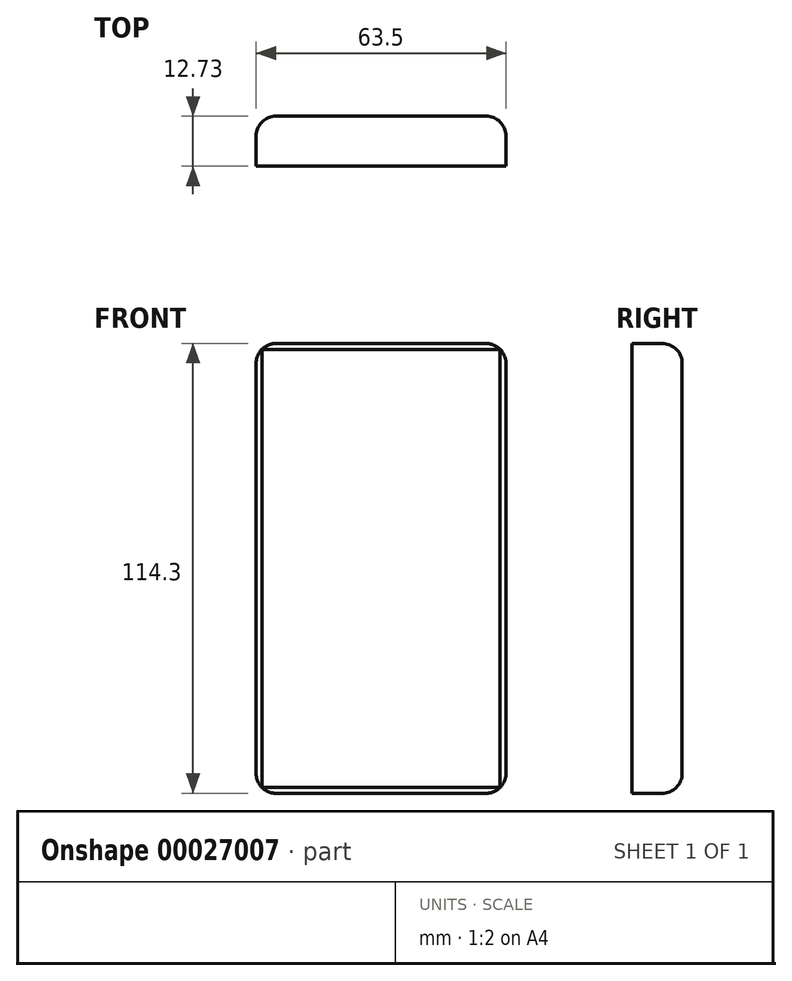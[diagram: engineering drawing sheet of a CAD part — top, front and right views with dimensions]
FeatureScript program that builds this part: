
annotation { "Feature Type Name" : "Feature", "Feature Type Description" : "" }
export const myFeature = defineFeature(function(context is Context, id is Id, definition is map)
    precondition{}
    {
        {
            var Q0;
            Q0=qCreatedBy(makeId("Front.planeOp"),FACE);
            var sketch = newSketch(context, id + "F0", { "sketchPlane" : qUnion([Q0])});
            skLineSegment(sketch, "E0.bottom", {"start": v(-36.96, 45.78) * mm, "end": v(26.54, 45.78) * mm});
            skLineSegment(sketch, "E0.top", {"start": v(-36.96, -68.52) * mm, "end": v(26.54, -68.52) * mm});
            skLineSegment(sketch, "E0.left", {"start": v(-36.96, 45.78) * mm, "end": v(-36.96, -68.52) * mm});
            skLineSegment(sketch, "E0.right", {"start": v(26.54, 45.78) * mm, "end": v(26.54, -68.52) * mm});
            skSolve(sketch);
        }
        {
            var Q0;
            Q0=makeQuery(id+"F0.imprint","IMPRINT",FACE,{"disambiguationData":[TD([[makeQuery(id+"F0.imprint","IMPRINT",EDGE,{"derivedFrom":sQuery(id+"F0.wireOp",EDGE,"E0.bottom")}),-1.0]])]});
            extrude(context, id + "F1", {"entities" : qUnion([Q0]), "depth" : 12.7 * mm});
        }
        {
            var Q0;
            Q0=makeQuery(id+"F1.opExtrude","SWEPT_EDGE",EDGE,{"disambiguationData":[OSD([sQuery(id+"F0.wireOp",EDGE,"E0.bottom"),sQuery(id+"F0.wireOp",EDGE,"E0.right")])]});
            var Q1;
            Q1=makeQuery(id+"F1.opExtrude","SWEPT_EDGE",EDGE,{"disambiguationData":[OSD([sQuery(id+"F0.wireOp",EDGE,"E0.top"),sQuery(id+"F0.wireOp",EDGE,"E0.right")])]});
            var Q2;
            Q2=makeQuery(id+"F1.opExtrude","SWEPT_EDGE",EDGE,{"disambiguationData":[OSD([sQuery(id+"F0.wireOp",EDGE,"E0.top"),sQuery(id+"F0.wireOp",EDGE,"E0.left")])]});
            var Q3;
            Q3=makeQuery(id+"F1.opExtrude","SWEPT_EDGE",EDGE,{"disambiguationData":[OSD([sQuery(id+"F0.wireOp",EDGE,"E0.bottom"),sQuery(id+"F0.wireOp",EDGE,"E0.left")])]});
            fillet(context, id + "F2", {"entities" : qUnion([Q0, Q1, Q2, Q3]), "radius" : 5.08 * mm, "allowEdgeOverflow" : false});
        }
        {
            var Q0;
            Q0=makeQuery(id+"F1.opExtrude","CAP_EDGE",EDGE,{"disambiguationData":[OSD([sQuery(id+"F0.wireOp",EDGE,"E0.right")])],"isStart":true});
            fillet(context, id + "F3", {"entities" : qUnion([Q0]), "radius" : 5.08 * mm, "tangentPropagation" : true, "allowEdgeOverflow" : false});
        }
        {
            var Q0;
            Q0=makeQuery(id+"F1.opExtrude","CAP_FACE",FACE,{"disambiguationData":[OSD([sQuery(id+"F0.wireOp",EDGE,"E0.bottom"),sQuery(id+"F0.wireOp",EDGE,"E0.top"),sQuery(id+"F0.wireOp",EDGE,"E0.left"),sQuery(id+"F0.wireOp",EDGE,"E0.right")])],"isStart":false});
            var sketch = newSketch(context, id + "F4", { "sketchPlane" : qUnion([Q0])});
            skLineSegment(sketch, "E1.bottom", {"start": v(-35.47, 44.29) * mm, "end": v(25.05, 44.29) * mm});
            skLineSegment(sketch, "E1.top", {"start": v(-35.47, -67.03) * mm, "end": v(25.05, -67.03) * mm});
            skLineSegment(sketch, "E1.left", {"start": v(-35.47, 44.29) * mm, "end": v(-35.47, -67.03) * mm});
            skLineSegment(sketch, "E1.right", {"start": v(25.05, 44.29) * mm, "end": v(25.05, -67.03) * mm});
            skSolve(sketch);
        }
        {
            var Q0;
            Q0=makeQuery(id+"F4.imprint","IMPRINT",FACE,{"disambiguationData":[TD([[makeQuery(id+"F4.imprint","IMPRINT",EDGE,{"derivedFrom":sQuery(id+"F4.wireOp",EDGE,"E1.bottom")}),-1.0]])]});
            extrude(context, id + "F5", {"entities" : qUnion([Q0]), "operationType" : NewBodyOperationType.ADD, "depth" : 0.03 * mm});
        }
        {
            var Q0;
            Q0=makeQuery(id+"F5.opExtrude","CAP_EDGE",EDGE,{"disambiguationData":[OSD([sQuery(id+"F4.wireOp",EDGE,"E1.right")])],"isStart":false});
            fillet(context, id + "F6", {"entities" : qUnion([Q0]), "radius" : 5.08 * mm, "tangentPropagation" : true, "allowEdgeOverflow" : false});
        }
    });
